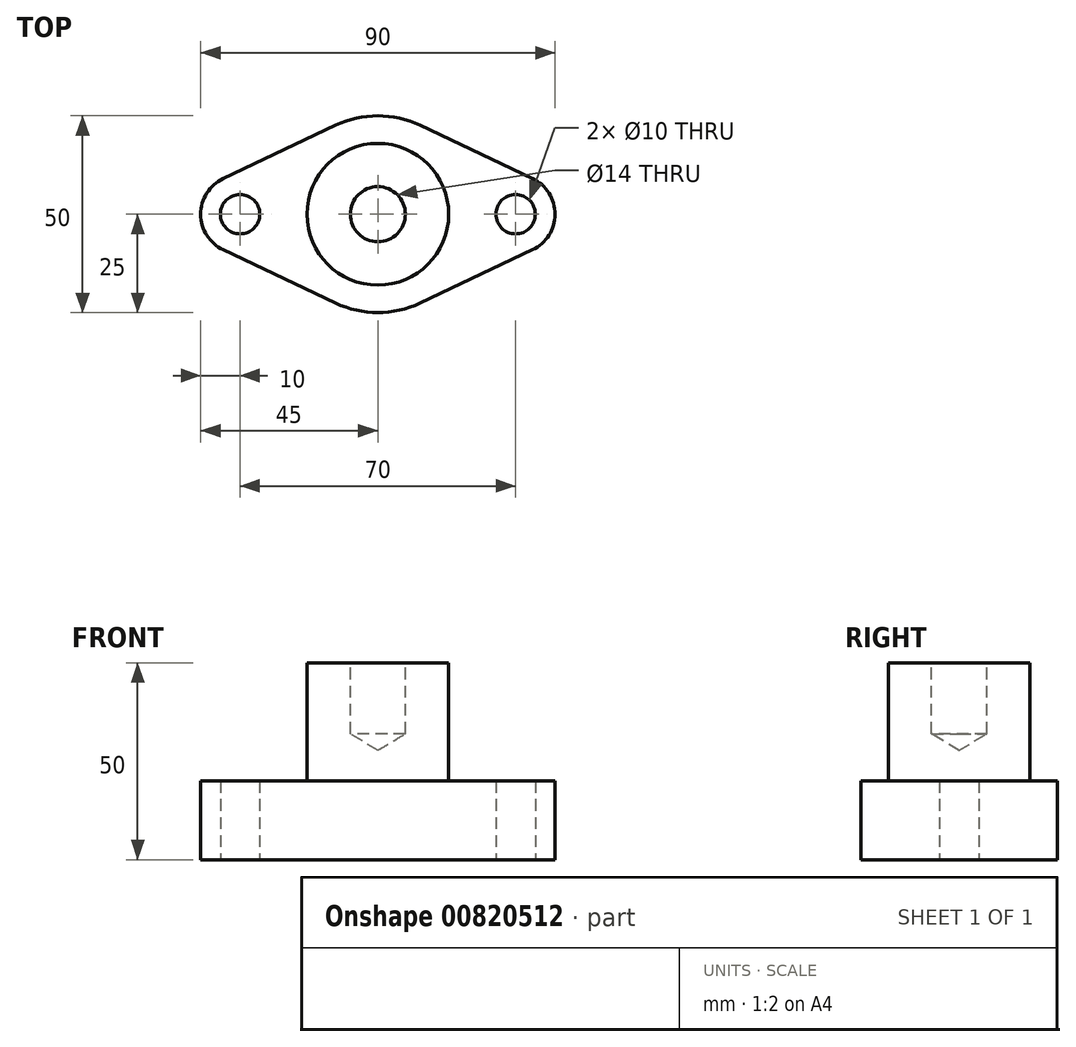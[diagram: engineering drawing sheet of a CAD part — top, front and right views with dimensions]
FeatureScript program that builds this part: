
annotation { "Feature Type Name" : "Feature", "Feature Type Description" : "" }
export const myFeature = defineFeature(function(context is Context, id is Id, definition is map)
    precondition{}
    {
        {
            var Q0;
            Q0=qCreatedBy(makeId("Top.planeOp"),FACE);
            var sketch = newSketch(context, id + "F0", { "sketchPlane" : qUnion([Q0])});
            skCircle(sketch, "E0", {"center": v(0, 0) * mm, "radius": 25 * mm});
            skPoint(sketch, "E1", {"position": v(-35, 0) * mm});
            skPoint(sketch, "E2", {"position": v(35, 0) * mm});
            skCircle(sketch, "E3", {"center": v(-35, 0) * mm, "radius": 10 * mm});
            skCircle(sketch, "E4", {"center": v(35, 0) * mm, "radius": 10 * mm});
            skLineSegment(sketch, "E5", {"start": v(-39.29, 9.04) * mm, "end": v(-10.71, 22.59) * mm});
            skLineSegment(sketch, "E6", {"start": v(10.71, 22.59) * mm, "end": v(39.29, 9.04) * mm});
            skLineSegment(sketch, "E7", {"start": v(39.29, -9.04) * mm, "end": v(10.71, -22.59) * mm});
            skLineSegment(sketch, "E8", {"start": v(-39.29, -9.04) * mm, "end": v(-10.71, -22.59) * mm});
            skSolve(sketch);
        }
        {
            var Q0;
            {var subQ0=sQuery(id+"F0.wireOp",EDGE,"E7");Q0=makeQuery(id+"F0.imprint","IMPRINT",FACE,{"disambiguationData":[TD([[makeQuery(id+"F0.imprint","IMPRINT",EDGE,{"derivedFrom":subQ0}),-1.0]])]});}
            var Q1;
            {var subQ0=sQuery(id+"F0.wireOp",EDGE,"E6");Q1=makeQuery(id+"F0.imprint","IMPRINT",FACE,{"disambiguationData":[TD([[makeQuery(id+"F0.imprint","IMPRINT",EDGE,{"derivedFrom":subQ0}),-1.0]])]});}
            var Q2;
            {var subQ0=sQuery(id+"F0.wireOp",EDGE,"E5");Q2=makeQuery(id+"F0.imprint","IMPRINT",FACE,{"disambiguationData":[TD([[makeQuery(id+"F0.imprint","IMPRINT",EDGE,{"derivedFrom":subQ0}),-1.0]])]});}
            var Q3;
            {var subQ0=sQuery(id+"F0.wireOp",EDGE,"E8");Q3=makeQuery(id+"F0.imprint","IMPRINT",FACE,{"disambiguationData":[TD([[makeQuery(id+"F0.imprint","IMPRINT",EDGE,{"derivedFrom":subQ0}),1.0]])]});}
            var Q4;
            {var subQ0=sQuery(id+"F0.wireOp",EDGE,"E3");var subQ1=makeQuery(id+"F0.imprint","INTERSECT",VERTEX,{"derivedFrom":[subQ0,sQuery(id+"F0.wireOp",EDGE,"E5")]});Q4=makeQuery(id+"F0.imprint","IMPRINT",FACE,{"disambiguationData":[TD([[makeQuery(id+"F0.imprint","IMPRINT",EDGE,{"disambiguationData":[TD([[subQ1,1.0]])],"derivedFrom":subQ0}),1.0]])]});}
            var Q5;
            {var subQ0=sQuery(id+"F0.wireOp",EDGE,"E4");var subQ1=makeQuery(id+"F0.imprint","INTERSECT",VERTEX,{"derivedFrom":[subQ0,sQuery(id+"F0.wireOp",EDGE,"E6")]});Q5=makeQuery(id+"F0.imprint","IMPRINT",FACE,{"disambiguationData":[TD([[makeQuery(id+"F0.imprint","IMPRINT",EDGE,{"disambiguationData":[TD([[subQ1,-1.0]])],"derivedFrom":subQ0}),1.0]])]});}
            var Q6;
            {var subQ0=sQuery(id+"F0.wireOp",EDGE,"E0");var subQ4=makeQuery(id+"F0.imprint","INTERSECT",VERTEX,{"derivedFrom":[subQ0,sQuery(id+"F0.wireOp",EDGE,"E6")]});Q6=makeQuery(id+"F0.imprint","IMPRINT",FACE,{"disambiguationData":[TD([[makeQuery(id+"F0.imprint","IMPRINT",EDGE,{"disambiguationData":[TD([[subQ4,1.0]])],"derivedFrom":subQ0}),1.0]])]});}
            extrude(context, id + "F1", {"entities" : qUnion([Q0, Q1, Q2, Q3, Q4, Q5, Q6]), "depth" : 20 * mm, "offsetDistance" : 25 * mm});
        }
        {
            var Q0;
            Q0=makeQuery(id+"F1.opExtrude","CAP_FACE",FACE,{"disambiguationData":[OSD([sQuery(id+"F0.wireOp",EDGE,"E0"),sQuery(id+"F0.wireOp",EDGE,"E3"),sQuery(id+"F0.wireOp",EDGE,"E4"),sQuery(id+"F0.wireOp",EDGE,"E5"),sQuery(id+"F0.wireOp",EDGE,"E6"),sQuery(id+"F0.wireOp",EDGE,"E7"),sQuery(id+"F0.wireOp",EDGE,"E8")])],"isStart":true});
            var sketch = newSketch(context, id + "F2", { "sketchPlane" : qUnion([Q0])});
            skPoint(sketch, "E9", {"position": v(-35, 0) * mm});
            skPoint(sketch, "E10", {"position": v(35, 0) * mm});
            skSolve(sketch);
        }
        {
            var Q0;
            Q0=sQuery(id+"F2.wireOp",VERTEX,"E9");
            var Q1;
            Q1=sQuery(id+"F2.wireOp",VERTEX,"E10");
            var Q2;
            Q2=makeQuery(id+"F1.opExtrude","SWEPT_BODY",BODY,{"disambiguationData":[OSD([sQuery(id+"F0.wireOp",EDGE,"E0"),sQuery(id+"F0.wireOp",EDGE,"E3"),sQuery(id+"F0.wireOp",EDGE,"E4"),sQuery(id+"F0.wireOp",EDGE,"E5"),sQuery(id+"F0.wireOp",EDGE,"E6"),sQuery(id+"F0.wireOp",EDGE,"E7"),sQuery(id+"F0.wireOp",EDGE,"E8")])]});
            hole(context, id + "F3", {"style" : HoleStyle.SIMPLE, "endStyle" : HoleEndStyle.THROUGH, "holeDiameter" : 10 * mm, "majorDiameter" : 5 * mm, "isTappedThrough" : true, "tappedDepth" : 12 * mm, "tapClearance" : 3, "locations" : qUnion([Q0, Q1]), "scope" : qUnion([Q2])});
        }
        {
            var Q0;
            Q0=makeQuery(id+"F1.opExtrude","CAP_FACE",FACE,{"disambiguationData":[OSD([sQuery(id+"F0.wireOp",EDGE,"E0"),sQuery(id+"F0.wireOp",EDGE,"E3"),sQuery(id+"F0.wireOp",EDGE,"E4"),sQuery(id+"F0.wireOp",EDGE,"E5"),sQuery(id+"F0.wireOp",EDGE,"E6"),sQuery(id+"F0.wireOp",EDGE,"E7"),sQuery(id+"F0.wireOp",EDGE,"E8")])],"isStart":false});
            var sketch = newSketch(context, id + "F4", { "sketchPlane" : qUnion([Q0])});
            skPoint(sketch, "E11", {"position": v(0, 0) * mm});
            skCircle(sketch, "E12", {"center": v(0, 0) * mm, "radius": 18 * mm});
            skSolve(sketch);
        }
        {
            var Q0;
            Q0=makeQuery(id+"F4.imprint","IMPRINT",FACE,{"disambiguationData":[TD([[makeQuery(id+"F4.imprint","IMPRINT",EDGE,{"derivedFrom":sQuery(id+"F4.wireOp",EDGE,"E12")}),1.0]])]});
            extrude(context, id + "F5", {"entities" : qUnion([Q0]), "operationType" : NewBodyOperationType.ADD, "depth" : 30 * mm, "offsetDistance" : 25 * mm});
        }
        {
            var Q0;
            Q0=makeQuery(id+"F5.opExtrude","CAP_FACE",FACE,{"disambiguationData":[OSD([sQuery(id+"F4.wireOp",EDGE,"E12")])],"isStart":false});
            var sketch = newSketch(context, id + "F6", { "sketchPlane" : qUnion([Q0])});
            skPoint(sketch, "E13", {"position": v(0, 0) * mm});
            skSolve(sketch);
        }
        {
            var Q0;
            Q0=sQuery(id+"F6.wireOp",VERTEX,"E13");
            var Q1;
            Q1=makeQuery(id+"F1.opExtrude","SWEPT_BODY",BODY,{"disambiguationData":[OSD([sQuery(id+"F0.wireOp",EDGE,"E0"),sQuery(id+"F0.wireOp",EDGE,"E3"),sQuery(id+"F0.wireOp",EDGE,"E4"),sQuery(id+"F0.wireOp",EDGE,"E5"),sQuery(id+"F0.wireOp",EDGE,"E6"),sQuery(id+"F0.wireOp",EDGE,"E7"),sQuery(id+"F0.wireOp",EDGE,"E8")])]});
            hole(context, id + "F7", {"style" : HoleStyle.SIMPLE, "endStyle" : HoleEndStyle.BLIND, "standardTappedOrClearance" : lookupTablePath({ "standard" : "ISO", "engagement" : "75%", "pitch" : "2 mm", "size" : "M16", "type" : "Tapped" }), "standardBlindInLast" : lookupTablePath({ "standard" : "ISO", "engagement" : "75%", "pitch" : "2 mm", "size" : "M16", "type" : "Tapped" }), "holeDiameter" : 14 * mm, "majorDiameter" : 16 * mm, "showTappedDepth" : true, "holeDepth" : 18 * mm, "isTappedThrough" : true, "tappedDepth" : 12 * mm, "tapClearance" : 3, "locations" : qUnion([Q0]), "scope" : qUnion([Q1])});
        }
    });
